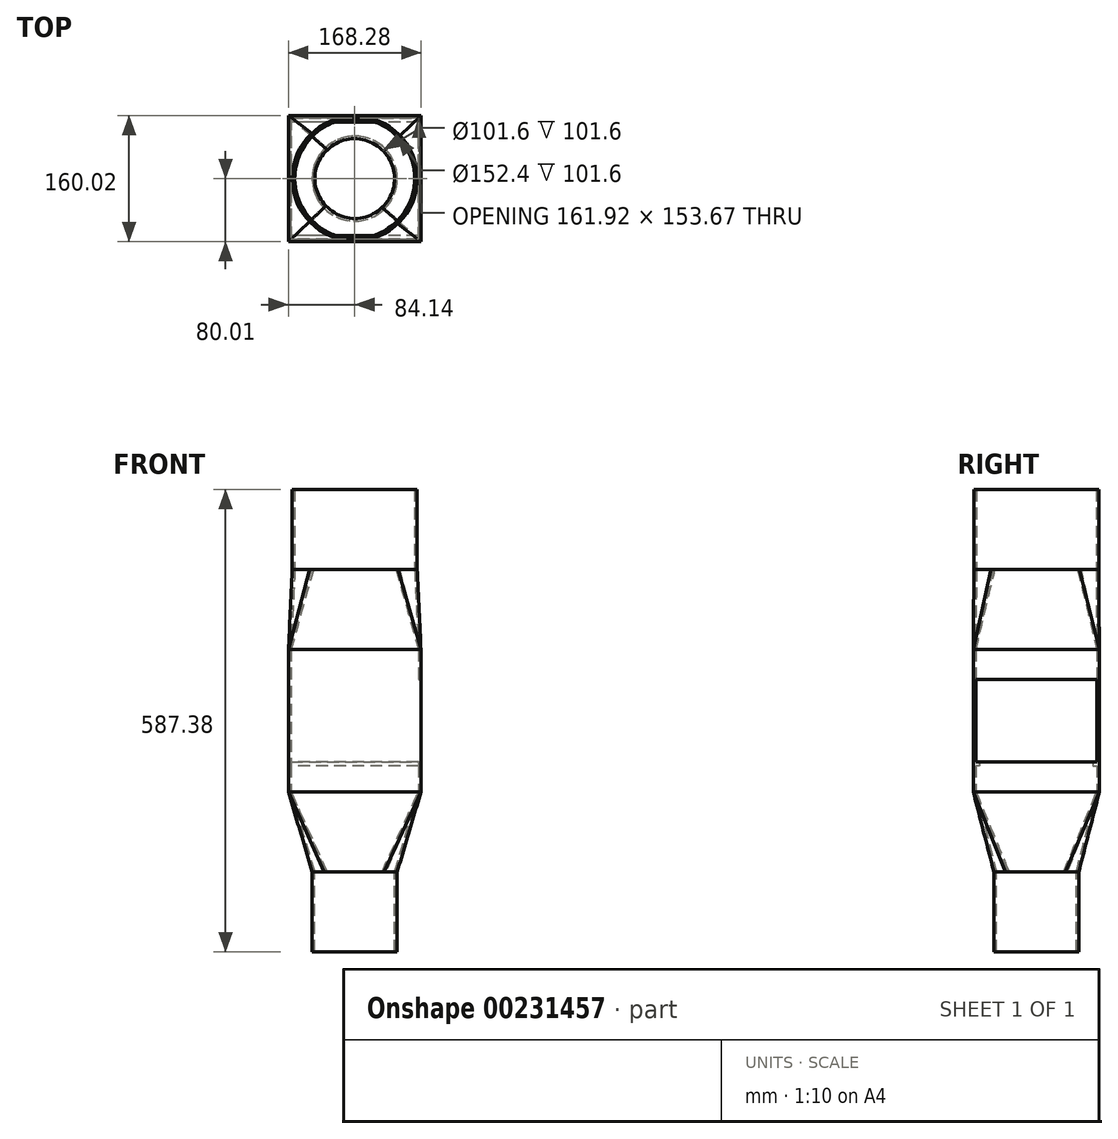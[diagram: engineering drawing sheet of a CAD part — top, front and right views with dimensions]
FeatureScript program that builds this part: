
annotation { "Feature Type Name" : "Feature", "Feature Type Description" : "" }
export const myFeature = defineFeature(function(context is Context, id is Id, definition is map)
    precondition{}
    {
        {
            var Q0;
            Q0=qCreatedBy(makeId("Top.planeOp"),FACE);
            var sketch = newSketch(context, id + "F0", { "sketchPlane" : qUnion([Q0])});
            skLineSegment(sketch, "E0.bottom", {"start": v(80.96, -76.83) * mm, "end": v(-80.96, -76.83) * mm});
            skLineSegment(sketch, "E0.top", {"start": v(80.96, 76.84) * mm, "end": v(-80.96, 76.83) * mm});
            skLineSegment(sketch, "E0.left", {"start": v(80.96, -76.83) * mm, "end": v(80.96, 76.84) * mm});
            skLineSegment(sketch, "E0.right", {"start": v(-80.96, -76.83) * mm, "end": v(-80.96, 76.83) * mm});
            skPoint(sketch, "E0.middle", {"position": v(0, 0) * mm});
            skLineSegment(sketch, "E1.0", {"start": v(-84.14, -80) * mm, "end": v(-84.14, 80) * mm});
            skLineSegment(sketch, "E1.1", {"start": v(84.14, -80) * mm, "end": v(-84.14, -80) * mm});
            skLineSegment(sketch, "E1.2", {"start": v(84.14, -80) * mm, "end": v(84.14, 80.01) * mm});
            skLineSegment(sketch, "E1.3", {"start": v(84.14, 80.01) * mm, "end": v(-84.14, 80) * mm});
            skSolve(sketch);
        }
        {
            var Q0;
            Q0=qSketchRegion(id+"F0",true);
            extrude(context, id + "F1", {"entities" : qUnion([Q0]), "depth" : 609.6 * mm});
        }
        {
            var Q0;
            Q0=makeQuery(id+"F1.opExtrude","SWEPT_FACE",FACE,{"disambiguationData":[OSD([sQuery(id+"F0.wireOp",EDGE,"E1.2")])]});
            var sketch = newSketch(context, id + "F2", { "sketchPlane" : qUnion([Q0])});
            skLineSegment(sketch, "E2.0", {"start": v(76.84, 419.1) * mm, "end": v(-76.83, 419.1) * mm});
            skLineSegment(sketch, "E3", {"start": v(-76.83, 419.1) * mm, "end": v(-76.83, 314.32) * mm});
            skLineSegment(sketch, "E4", {"start": v(-76.83, 314.32) * mm, "end": v(76.84, 314.32) * mm});
            skLineSegment(sketch, "E5", {"start": v(76.84, 314.32) * mm, "end": v(76.83, 419.1) * mm});
            skSolve(sketch);
        }
        {
            var Q0;
            Q0=qSketchRegion(id+"F2",true);
            extrude(context, id + "F3", {"entities" : qUnion([Q0]), "operationType" : NewBodyOperationType.REMOVE, "oppositeDirection" : true, "depth" : 25.4 * mm});
        }
        {
            var Q0;
            Q0=makeQuery(id+"F3.boolean.opBoolean","MERGE",FACE,{"derivedFrom":[makeQuery(id+"FJlKoGUUFFQVLLg_1.boolean.opBoolean","MERGE",FACE,{"derivedFrom":[makeQuery(id+"F1.opExtrude","SWEPT_FACE",FACE,{"disambiguationData":[OSD([sQuery(id+"F0.wireOp",EDGE,"E0.bottom")])]}),makeQuery(id+"FJlKoGUUFFQVLLg_1.opExtrude","SWEPT_FACE",FACE,{"disambiguationData":[OSD([sQuery(id+"FDuAmRhbZzFj5Qb_1.wireOp",EDGE,"6e817850-069e-4b5f-8f8a-194da3d11760.0")])]})]}),makeQuery(id+"F3.opExtrude","SWEPT_FACE",FACE,{"disambiguationData":[OSD([sQuery(id+"F2.wireOp",EDGE,"E3")])]})]});
            var sketch = newSketch(context, id + "F4", { "sketchPlane" : qUnion([Q0])});
            skLineSegment(sketch, "E6.0", {"start": v(-80.96, 314.32) * mm, "end": v(-84.14, 314.32) * mm});
            skLineSegment(sketch, "E7.bottom", {"start": v(-80.96, 314.32) * mm, "end": v(80.96, 314.32) * mm});
            skLineSegment(sketch, "E7.top", {"start": v(-80.96, 309.56) * mm, "end": v(80.96, 309.56) * mm});
            skLineSegment(sketch, "E7.left", {"start": v(-80.96, 314.32) * mm, "end": v(-80.96, 309.56) * mm});
            skLineSegment(sketch, "E7.right", {"start": v(80.96, 314.32) * mm, "end": v(80.96, 309.56) * mm});
            skLineSegment(sketch, "E8", {"start": v(-76.2, 314.32) * mm, "end": v(-76.2, 309.56) * mm});
            skSolve(sketch);
        }
        {
            var Q0;
            {var subQ0=sQuery(id+"F4.wireOp",EDGE,"E7.right");Q0=makeQuery(id+"F4.imprint","IMPRINT",FACE,{"disambiguationData":[TD([[makeQuery(id+"F4.imprint","IMPRINT",EDGE,{"derivedFrom":subQ0}),-1.0]])]});}
            var Q1;
            {var subQ0=sQuery(id+"F4.wireOp",EDGE,"E7.left");Q1=makeQuery(id+"F4.imprint","IMPRINT",FACE,{"disambiguationData":[TD([[makeQuery(id+"F4.imprint","IMPRINT",EDGE,{"derivedFrom":subQ0}),1.0]])]});}
            extrude(context, id + "F5", {"entities" : qUnion([Q0, Q1]), "operationType" : NewBodyOperationType.ADD, "depth" : 4.76 * mm});
        }
        {
            var Q0;
            Q0=makeQuery(id+"F3.boolean.opBoolean","MERGE",FACE,{"derivedFrom":[makeQuery(id+"FJlKoGUUFFQVLLg_1.boolean.opBoolean","MERGE",FACE,{"derivedFrom":[makeQuery(id+"F1.opExtrude","SWEPT_FACE",FACE,{"disambiguationData":[OSD([sQuery(id+"F0.wireOp",EDGE,"E0.top")])]}),makeQuery(id+"FJlKoGUUFFQVLLg_1.opExtrude","SWEPT_FACE",FACE,{"disambiguationData":[OSD([sQuery(id+"FDuAmRhbZzFj5Qb_1.wireOp",EDGE,"e46d9115-ca44-42dd-b1b8-e05000f95a17.0")])]})]}),makeQuery(id+"F3.opExtrude","SWEPT_FACE",FACE,{"disambiguationData":[OSD([sQuery(id+"F2.wireOp",EDGE,"E5")])]})]});
            var sketch = newSketch(context, id + "F6", { "sketchPlane" : qUnion([Q0])});
            skLineSegment(sketch, "E9.0", {"start": v(80.96, 314.32) * mm, "end": v(84.14, 314.32) * mm});
            skLineSegment(sketch, "E10.bottom", {"start": v(80.96, 314.32) * mm, "end": v(-80.96, 314.32) * mm});
            skLineSegment(sketch, "E10.top", {"start": v(80.96, 309.56) * mm, "end": v(-80.96, 309.56) * mm});
            skLineSegment(sketch, "E10.left", {"start": v(80.96, 314.32) * mm, "end": v(80.96, 309.56) * mm});
            skLineSegment(sketch, "E10.right", {"start": v(-80.96, 314.32) * mm, "end": v(-80.96, 309.56) * mm});
            skLineSegment(sketch, "E11", {"start": v(76.2, 309.56) * mm, "end": v(76.2, 314.32) * mm});
            skPoint(sketch, "E11.endSnap0", {"position": v(82.55, 314.32) * mm});
            skSolve(sketch);
        }
        {
            var Q0;
            {var subQ0=sQuery(id+"F6.wireOp",EDGE,"E10.right");Q0=makeQuery(id+"F6.imprint","IMPRINT",FACE,{"disambiguationData":[TD([[makeQuery(id+"F6.imprint","IMPRINT",EDGE,{"derivedFrom":subQ0}),1.0]])]});}
            var Q1;
            {var subQ0=sQuery(id+"F6.wireOp",EDGE,"E10.left");Q1=makeQuery(id+"F6.imprint","IMPRINT",FACE,{"disambiguationData":[TD([[makeQuery(id+"F6.imprint","IMPRINT",EDGE,{"derivedFrom":subQ0}),-1.0]])]});}
            extrude(context, id + "F7", {"entities" : qUnion([Q0, Q1]), "operationType" : NewBodyOperationType.ADD, "depth" : 4.76 * mm});
        }
        {
            var Q0;
            Q0=makeQuery(id+"F1.opExtrude","SWEPT_FACE",FACE,{"disambiguationData":[OSD([sQuery(id+"F0.wireOp",EDGE,"E1.2")])]});
            var sketch = newSketch(context, id + "F8", { "sketchPlane" : qUnion([Q0])});
            skLineSegment(sketch, "E12.bottom", {"start": v(-105.41, 457.2) * mm, "end": v(105.4, 457.2) * mm});
            skLineSegment(sketch, "E12.top", {"start": v(-105.41, 635) * mm, "end": v(105.4, 635) * mm});
            skLineSegment(sketch, "E12.left", {"start": v(-105.41, 457.2) * mm, "end": v(-105.41, 635) * mm});
            skLineSegment(sketch, "E12.right", {"start": v(105.4, 457.2) * mm, "end": v(105.4, 635) * mm});
            skLineSegment(sketch, "E13.bottom", {"start": v(-105.41, 276.22) * mm, "end": v(105.4, 276.22) * mm});
            skLineSegment(sketch, "E13.top", {"start": v(-105.4, -25.4) * mm, "end": v(105.41, -25.4) * mm});
            skLineSegment(sketch, "E13.left", {"start": v(-105.41, 276.22) * mm, "end": v(-105.4, -25.4) * mm});
            skLineSegment(sketch, "E13.right", {"start": v(105.4, 276.22) * mm, "end": v(105.41, -25.4) * mm});
            skSolve(sketch);
        }
        {
            var Q0;
            Q0 = qSketchRegion(id + "F8", true);
            extrude(context, id + "F9", {"entities" : qUnion([Q0]), "operationType" : NewBodyOperationType.REMOVE, "endBound" : BoundingType.THROUGH_ALL, "oppositeDirection" : true, "depth" : 25.4 * mm});
        }
        {
            var Q0;
            Q0=makeQuery(id+"F9.boolean.opBoolean","COPY",FACE,{"derivedFrom":makeQuery(id+"F9.opExtrude","SWEPT_FACE",FACE,{"disambiguationData":[OSD([sQuery(id+"F8.wireOp",EDGE,"E12.bottom")])]})});
            cPlane(context, id + "F10", {"entities" : qUnion([Q0]), "cplaneType" : CPlaneType.OFFSET, "offset" : 101.6 * mm, "width" : 152.4 * mm, "height" : 152.4 * mm});
        }
        {
            var Q0;
            Q0=makeQuery(id+"F9.boolean.opBoolean","COPY",FACE,{"derivedFrom":makeQuery(id+"F9.opExtrude","SWEPT_FACE",FACE,{"disambiguationData":[OSD([sQuery(id+"F8.wireOp",EDGE,"E13.bottom")])]})});
            cPlane(context, id + "F11", {"entities" : qUnion([Q0]), "cplaneType" : CPlaneType.OFFSET, "offset" : 101.6 * mm, "width" : 152.4 * mm, "height" : 152.4 * mm});
        }
        {
            var Q0;
            Q0=qCreatedBy(id+"F10.planeOp",FACE);
            var sketch = newSketch(context, id + "F12", { "sketchPlane" : qUnion([Q0])});
            skCircle(sketch, "E14", {"center": v(0, 0) * mm, "radius": 76.2 * mm});
            skCircle(sketch, "E15.0", {"center": v(0, 0) * mm, "radius": 79.38 * mm});
            skSolve(sketch);
        }
        {
            var Q0;
            Q0 = qSketchRegion(id + "F12", true);
            extrude(context, id + "F13", {"entities" : qUnion([Q0]), "depth" : 101.6 * mm});
        }
        {
            var Q0;
            Q0=qCreatedBy(id+"F11.planeOp",FACE);
            var sketch = newSketch(context, id + "F14", { "sketchPlane" : qUnion([Q0])});
            skCircle(sketch, "E16", {"center": v(0, 0) * mm, "radius": 50.8 * mm});
            skCircle(sketch, "E17.0", {"center": v(0, 0) * mm, "radius": 53.98 * mm});
            skSolve(sketch);
        }
        {
            var Q0;
            Q0 = qSketchRegion(id + "F14", true);
            extrude(context, id + "F15", {"entities" : qUnion([Q0]), "depth" : 101.6 * mm});
        }
        {
            var Q0;
            Q0=makeQuery(id+"F9.boolean.opBoolean","COPY",FACE,{"derivedFrom":makeQuery(id+"F9.opExtrude","SWEPT_FACE",FACE,{"disambiguationData":[OSD([sQuery(id+"F8.wireOp",EDGE,"E12.bottom")])]})});
            var sketch = newSketch(context, id + "F16", { "sketchPlane" : qUnion([Q0])});
            skLineSegment(sketch, "E18.0", {"start": v(84.14, -80) * mm, "end": v(84.14, 80.01) * mm});
            skLineSegment(sketch, "E19.0", {"start": v(-84.14, 80) * mm, "end": v(84.14, 80.01) * mm});
            skLineSegment(sketch, "E20.0", {"start": v(-84.14, 80) * mm, "end": v(-84.14, -80) * mm});
            skLineSegment(sketch, "E21.0", {"start": v(-84.14, -80) * mm, "end": v(84.14, -80) * mm});
            skSolve(sketch);
        }
        {
            var Q0;
            Q0=makeQuery(id+"F13.opExtrude","CAP_FACE",FACE,{"disambiguationData":[OSD([sQuery(id+"F12.wireOp",EDGE,"E14"),sQuery(id+"F12.wireOp",EDGE,"E15.0")])],"isStart":true});
            var sketch = newSketch(context, id + "F17", { "sketchPlane" : qUnion([Q0])});
            skCircle(sketch, "E22.0", {"center": v(0, 0) * mm, "radius": 79.38 * mm});
            skSolve(sketch);
        }
        {
            var Q0;
            Q0 = qSketchRegion(id + "F16", true);
            var Q1;
            Q1 = qSketchRegion(id + "F17", true);
            loft(context, id + "F18", {"sheetProfilesArray" : [{ "sheetProfileEntities" : qUnion([Q0]) }, { "sheetProfileEntities" : qUnion([Q1]) }]});
        }
        {
            var Q0;
            Q0=makeQuery(id+"F9.boolean.opBoolean","COPY",FACE,{"derivedFrom":makeQuery(id+"F9.opExtrude","SWEPT_FACE",FACE,{"disambiguationData":[OSD([sQuery(id+"F8.wireOp",EDGE,"E13.bottom")])]})});
            var sketch = newSketch(context, id + "F19", { "sketchPlane" : qUnion([Q0])});
            skLineSegment(sketch, "E23.0", {"start": v(-84.14, -80.01) * mm, "end": v(84.14, -80.01) * mm});
            skLineSegment(sketch, "E24.0", {"start": v(84.14, 80) * mm, "end": v(84.14, -80.01) * mm});
            skLineSegment(sketch, "E25.0", {"start": v(-84.14, 80) * mm, "end": v(84.14, 80) * mm});
            skLineSegment(sketch, "E26.0", {"start": v(-84.14, -80.01) * mm, "end": v(-84.14, 80) * mm});
            skSolve(sketch);
        }
        {
            var Q0;
            Q0=makeQuery(id+"F15.opExtrude","CAP_FACE",FACE,{"disambiguationData":[OSD([sQuery(id+"F14.wireOp",EDGE,"E16"),sQuery(id+"F14.wireOp",EDGE,"E17.0")])],"isStart":true});
            var sketch = newSketch(context, id + "F20", { "sketchPlane" : qUnion([Q0])});
            skCircle(sketch, "E27.0", {"center": v(0, 0) * mm, "radius": 53.98 * mm});
            skSolve(sketch);
        }
        {
            var Q0;
            Q0 = qSketchRegion(id + "F19", true);
            var Q1;
            Q1 = qSketchRegion(id + "F20", true);
            loft(context, id + "F21", {"sheetProfilesArray" : [{ "sheetProfileEntities" : qUnion([Q0]) }, { "sheetProfileEntities" : qUnion([Q1]) }]});
        }
        {
            var Q0;
            {var subQ0=makeQuery(id+"F9.opExtrude","SWEPT_FACE",FACE,{"disambiguationData":[OSD([sQuery(id+"F8.wireOp",EDGE,"E13.bottom")])]});var subQ1=sQuery(id+"F0.wireOp",EDGE,"E0.right");var subQ7=makeQuery(id+"F1.opExtrude","SWEPT_FACE",FACE,{"disambiguationData":[OSD([subQ1])]});Q0=makeQuery(id+"F21.opLoft","CAP_FACE",FACE,{"disambiguationData":[OSD([makeQuery(id+"F19.imprint","IMPRINT",FACE,{"disambiguationData":[TD([[makeQuery(id+"F19.imprint","IMPRINT",EDGE,{"derivedFrom":makeQuery(id+"F9.boolean.opBoolean","INTERSECT",EDGE,{"derivedFrom":[subQ7,subQ0]})}),-1.0]])]})])],"isStart":true});}
            var Q1;
            Q1=makeQuery(id+"F21.opLoft","CAP_FACE",FACE,{"disambiguationData":[OSD([makeQuery(id+"F20.imprint","IMPRINT",FACE,{"disambiguationData":[TD([[makeQuery(id+"F20.imprint","IMPRINT",EDGE,{"derivedFrom":makeQuery(id+"F15.opExtrude","CAP_EDGE",EDGE,{"disambiguationData":[OSD([sQuery(id+"F14.wireOp",EDGE,"E16")])],"isStart":true})}),-1.0]])]})])],"isStart":true});
            shell(context, id + "F22", {"entities" : qUnion([Q0, Q1]), "thickness" : 3.17 * mm});
        }
        {
            var Q0;
            {var subQ0=makeQuery(id+"F9.opExtrude","SWEPT_FACE",FACE,{"disambiguationData":[OSD([sQuery(id+"F8.wireOp",EDGE,"E12.bottom")])]});var subQ4=sQuery(id+"F0.wireOp",EDGE,"E0.right");var subQ13=makeQuery(id+"F1.opExtrude","SWEPT_FACE",FACE,{"disambiguationData":[OSD([subQ4])]});Q0=makeQuery(id+"F18.opLoft","CAP_FACE",FACE,{"disambiguationData":[OSD([makeQuery(id+"F16.imprint","IMPRINT",FACE,{"disambiguationData":[TD([[makeQuery(id+"F16.imprint","IMPRINT",EDGE,{"derivedFrom":makeQuery(id+"F9.boolean.opBoolean","INTERSECT",EDGE,{"derivedFrom":[subQ13,subQ0]})}),1.0]])]})])],"isStart":true});}
            var Q1;
            Q1=makeQuery(id+"F18.opLoft","CAP_FACE",FACE,{"disambiguationData":[OSD([makeQuery(id+"F17.imprint","IMPRINT",FACE,{"disambiguationData":[TD([[makeQuery(id+"F17.imprint","IMPRINT",EDGE,{"derivedFrom":makeQuery(id+"F13.opExtrude","CAP_EDGE",EDGE,{"disambiguationData":[OSD([sQuery(id+"F12.wireOp",EDGE,"E14")])],"isStart":true})}),-1.0]])]})])],"isStart":true});
            shell(context, id + "F23", {"entities" : qUnion([Q0, Q1]), "thickness" : 3.17 * mm});
        }
    });
